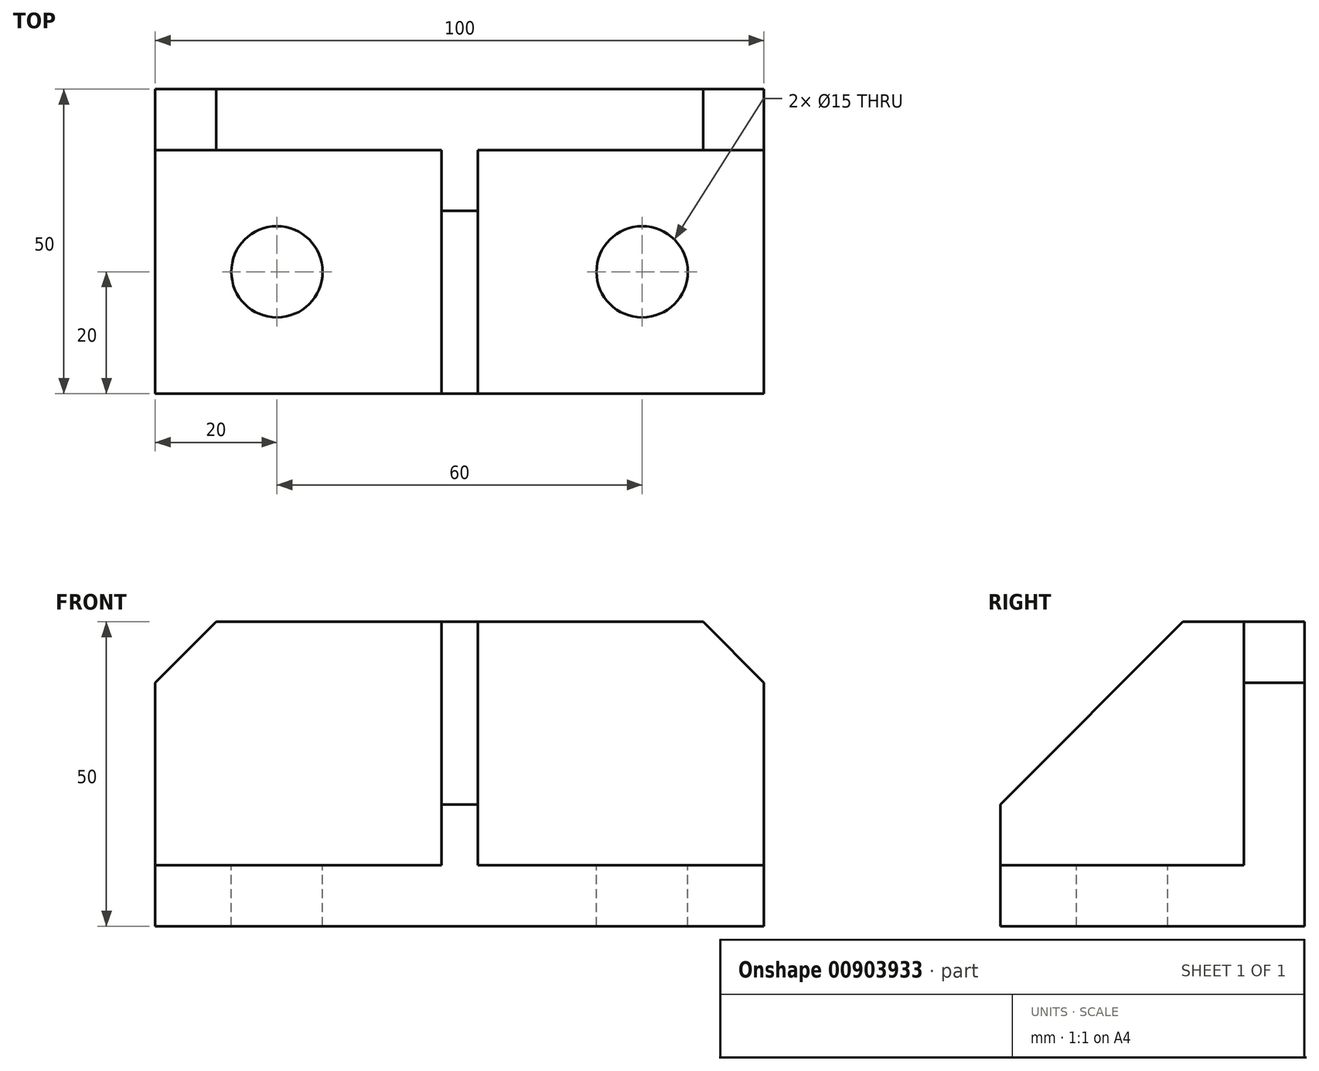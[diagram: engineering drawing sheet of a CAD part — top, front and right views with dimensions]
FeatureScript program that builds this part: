
annotation { "Feature Type Name" : "Feature", "Feature Type Description" : "" }
export const myFeature = defineFeature(function(context is Context, id is Id, definition is map)
    precondition{}
    {
        {
            var Q0;
            Q0=qCreatedBy(makeId("Top.planeOp"),FACE);
            var sketch = newSketch(context, id + "F0", { "sketchPlane" : qUnion([Q0])});
            skLineSegment(sketch, "E0.bottom", {"start": v(50, -25) * mm, "end": v(-50, -25) * mm});
            skLineSegment(sketch, "E0.top", {"start": v(50, 25) * mm, "end": v(-50, 25) * mm});
            skLineSegment(sketch, "E0.left", {"start": v(50, -25) * mm, "end": v(50, 25) * mm});
            skLineSegment(sketch, "E0.right", {"start": v(-50, -25) * mm, "end": v(-50, 25) * mm});
            skPoint(sketch, "E0.middle", {"position": v(0, 0) * mm});
            skSolve(sketch);
        }
        {
            var Q0;
            Q0=makeQuery(id+"F0.imprint","IMPRINT",FACE,{"disambiguationData":[TD([[makeQuery(id+"F0.imprint","IMPRINT",EDGE,{"derivedFrom":sQuery(id+"F0.wireOp",EDGE,"E0.bottom")}),-1.0]])]});
            extrude(context, id + "F1", {"entities" : qUnion([Q0]), "depth" : 50 * mm, "offsetDistance" : 25 * mm});
        }
        {
            var Q0;
            Q0=makeQuery(id+"F1.opExtrude","SWEPT_FACE",FACE,{"disambiguationData":[OSD([sQuery(id+"F0.wireOp",EDGE,"E0.left")])]});
            var Q1;
            Q1=makeQuery(id+"F1.opExtrude","CAP_FACE",FACE,{"disambiguationData":[OSD([sQuery(id+"F0.wireOp",EDGE,"E0.bottom"),sQuery(id+"F0.wireOp",EDGE,"E0.top"),sQuery(id+"F0.wireOp",EDGE,"E0.left"),sQuery(id+"F0.wireOp",EDGE,"E0.right")])],"isStart":false});
            var Q2;
            Q2=makeQuery(id+"F1.opExtrude","SWEPT_FACE",FACE,{"disambiguationData":[OSD([sQuery(id+"F0.wireOp",EDGE,"E0.bottom")])]});
            var Q3;
            Q3=makeQuery(id+"F1.opExtrude","SWEPT_FACE",FACE,{"disambiguationData":[OSD([sQuery(id+"F0.wireOp",EDGE,"E0.right")])]});
            shell(context, id + "F2", {"entities" : qUnion([Q0, Q1, Q2, Q3]), "thickness" : 10 * mm});
        }
        {
            var Q0;
            Q0=makeQuery(id+"F2.opShell","OFFSET_FACE",FACE,{"disambiguationData":[OSD([sQuery(id+"F0.wireOp",EDGE,"E0.bottom"),sQuery(id+"F0.wireOp",EDGE,"E0.top"),sQuery(id+"F0.wireOp",EDGE,"E0.left"),sQuery(id+"F0.wireOp",EDGE,"E0.right")])]});
            var sketch = newSketch(context, id + "F3", { "sketchPlane" : qUnion([Q0])});
            skLineSegment(sketch, "E1.0", {"start": v(50, -5) * mm, "end": v(-50, -5) * mm, "construction": true});
            skLineSegment(sketch, "E2.0", {"start": v(55, -30) * mm, "end": v(55, 20) * mm});
            skLineSegment(sketch, "E2.1", {"start": v(-55, -30) * mm, "end": v(55, -30) * mm});
            skLineSegment(sketch, "E2.2", {"start": v(-55, 20) * mm, "end": v(-55, -30) * mm});
            skLineSegment(sketch, "E2.3", {"start": v(55, 20) * mm, "end": v(-55, 20) * mm});
            skLineSegment(sketch, "E3.0", {"start": v(-30, -25) * mm, "end": v(-30, 15) * mm, "construction": true});
            skLineSegment(sketch, "E4.0", {"start": v(30, -25) * mm, "end": v(30, 15) * mm, "construction": true});
            skCircle(sketch, "E5", {"center": v(-30, -5) * mm, "radius": 7.5 * mm});
            skCircle(sketch, "E6", {"center": v(30, -5) * mm, "radius": 7.5 * mm});
            skSolve(sketch);
        }
        {
            var Q0;
            Q0=makeQuery(id+"F3.imprint","IMPRINT",FACE,{"disambiguationData":[TD([[makeQuery(id+"F3.imprint","IMPRINT",EDGE,{"derivedFrom":sQuery(id+"F3.wireOp",EDGE,"E5")}),1.0]])]});
            var Q1;
            Q1=makeQuery(id+"F3.imprint","IMPRINT",FACE,{"disambiguationData":[TD([[makeQuery(id+"F3.imprint","IMPRINT",EDGE,{"derivedFrom":sQuery(id+"F3.wireOp",EDGE,"E6")}),1.0]])]});
            extrude(context, id + "F4", {"entities" : qUnion([Q0, Q1]), "operationType" : NewBodyOperationType.REMOVE, "endBound" : BoundingType.THROUGH_ALL, "oppositeDirection" : true, "depth" : 25 * mm, "offsetDistance" : 25 * mm});
        }
        {
            var Q0;
            Q0=makeQuery(id+"F2.opShell","OFFSET_FACE",FACE,{"disambiguationData":[OSD([sQuery(id+"F0.wireOp",EDGE,"E0.bottom"),sQuery(id+"F0.wireOp",EDGE,"E0.top"),sQuery(id+"F0.wireOp",EDGE,"E0.left"),sQuery(id+"F0.wireOp",EDGE,"E0.right")])]});
            var sketch = newSketch(context, id + "F5", { "sketchPlane" : qUnion([Q0])});
            skLineSegment(sketch, "E7.bottom", {"start": v(-3, 15) * mm, "end": v(3, 15) * mm});
            skLineSegment(sketch, "E7.top", {"start": v(-3, -25) * mm, "end": v(3, -25) * mm});
            skLineSegment(sketch, "E7.left", {"start": v(-3, 15) * mm, "end": v(-3, -25) * mm});
            skLineSegment(sketch, "E7.right", {"start": v(3, 15) * mm, "end": v(3, -25) * mm});
            skSolve(sketch);
        }
        {
            var Q0;
            Q0=makeQuery(id+"F5.imprint","IMPRINT",FACE,{"disambiguationData":[TD([[makeQuery(id+"F5.imprint","IMPRINT",EDGE,{"derivedFrom":sQuery(id+"F5.wireOp",EDGE,"E7.bottom")}),1.0]])]});
            var Q1;
            Q1=makeQuery(id+"F1.opExtrude","CAP_FACE",FACE,{"disambiguationData":[OSD([sQuery(id+"F0.wireOp",EDGE,"E0.bottom"),sQuery(id+"F0.wireOp",EDGE,"E0.top"),sQuery(id+"F0.wireOp",EDGE,"E0.left"),sQuery(id+"F0.wireOp",EDGE,"E0.right")])],"isStart":false});
            extrude(context, id + "F6", {"entities" : qUnion([Q0]), "operationType" : NewBodyOperationType.ADD, "endBound" : BoundingType.UP_TO_SURFACE, "depth" : 25 * mm, "endBoundEntityFace" : qUnion([Q1]), "offsetDistance" : 25 * mm});
        }
        {
            var Q0;
            Q0=makeQuery(id+"F1.opExtrude","CAP_EDGE",EDGE,{"disambiguationData":[OSD([sQuery(id+"F0.wireOp",EDGE,"E0.left")])],"isStart":false});
            var Q1;
            Q1=makeQuery(id+"F1.opExtrude","CAP_EDGE",EDGE,{"disambiguationData":[OSD([sQuery(id+"F0.wireOp",EDGE,"E0.right")])],"isStart":false});
            chamfer(context, id + "F7", {"entities" : qUnion([Q0, Q1]), "width" : 10 * mm, "tangentPropagation" : true});
        }
        {
            var Q0;
            Q0=makeQuery(id+"F6.opExtrude","CAP_EDGE",EDGE,{"disambiguationData":[OSD([sQuery(id+"F5.wireOp",EDGE,"E7.top")])],"isStart":false});
            chamfer(context, id + "F8", {"entities" : qUnion([Q0]), "width" : 30 * mm, "tangentPropagation" : true});
        }
    });
